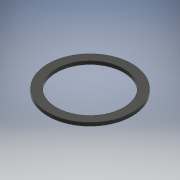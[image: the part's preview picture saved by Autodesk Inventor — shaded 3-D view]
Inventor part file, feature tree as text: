
AUTODESK INVENTOR PART (.ipt)
format: ipt  version: 2017 (Build 210142000, 142)  size: 99,328 bytes
history: native  units: mm
features: extrude x1, sketch x1
ambient origin geometry x8: Origin, YZ Plane, XZ Plane, XY Plane, X Axis, Y Axis, Z Axis, Center Point
bodies: Solid1 (feature_tree)
feature tree (2):
  extrude  "Extrusion1"  Depth=2.0mm
  sketch  "Sketch1"  dims[d0=50.0mm d1=40.0mm d2=2.0mm d3=0.0mm]
